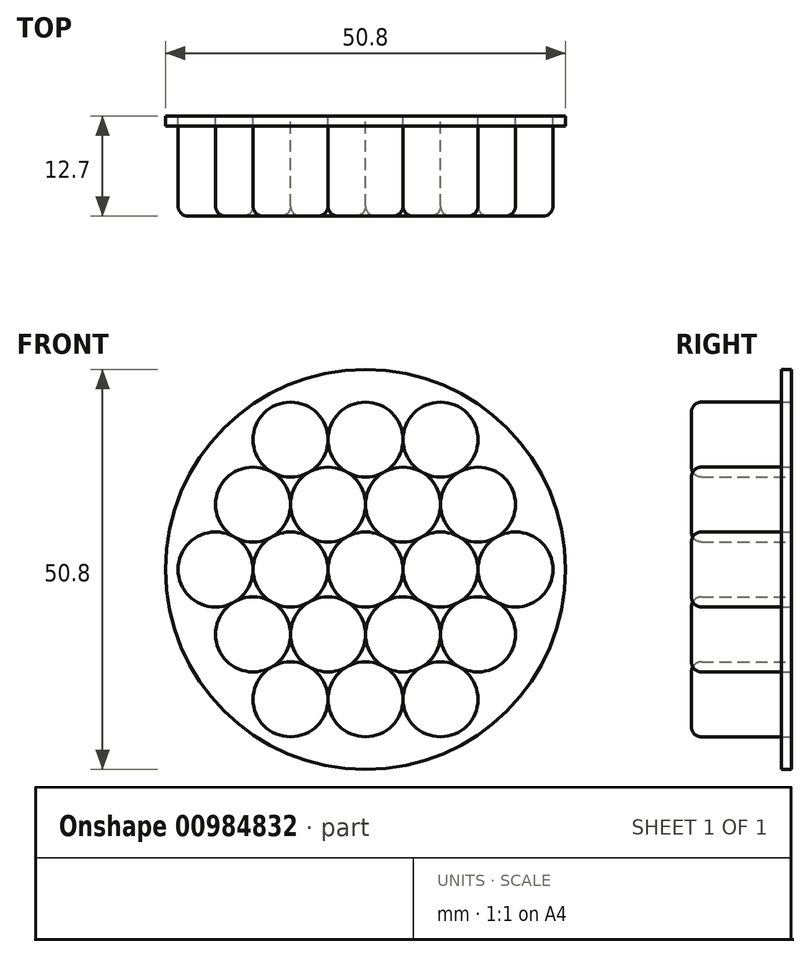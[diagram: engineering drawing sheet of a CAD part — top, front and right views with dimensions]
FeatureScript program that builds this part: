
annotation { "Feature Type Name" : "Feature", "Feature Type Description" : "" }
export const myFeature = defineFeature(function(context is Context, id is Id, definition is map)
    precondition{}
    {
        {
            var Q0;
            Q0=qCreatedBy(makeId("Front.planeOp"),FACE);
            var sketch = newSketch(context, id + "F0", { "sketchPlane" : qUnion([Q0])});
            skCircle(sketch, "E0", {"center": v(0, 0) * mm, "radius": 4.76 * mm});
            skCircle(sketch, "E1", {"center": v(-9.53, 0) * mm, "radius": 4.76 * mm});
            skCircle(sketch, "E2.1.0", {"center": v(-4.76, -8.25) * mm, "radius": 4.76 * mm});
            skCircle(sketch, "E2.2.0", {"center": v(4.76, -8.25) * mm, "radius": 4.76 * mm});
            skCircle(sketch, "E3.1.3.0", {"center": v(9.53, 0) * mm, "radius": 4.76 * mm});
            skCircle(sketch, "E3.1.4.0", {"center": v(4.76, 8.25) * mm, "radius": 4.76 * mm});
            skCircle(sketch, "E3.1.5.0", {"center": v(-4.76, 8.25) * mm, "radius": 4.76 * mm});
            skCircle(sketch, "E4.1.0", {"center": v(-14.29, 8.25) * mm, "radius": 4.76 * mm});
            skCircle(sketch, "E4.2.0", {"center": v(-9.53, 16.5) * mm, "radius": 4.76 * mm});
            skCircle(sketch, "E5.1.0", {"center": v(0, 16.5) * mm, "radius": 4.76 * mm});
            skCircle(sketch, "E5.2.0", {"center": v(9.53, 16.5) * mm, "radius": 4.76 * mm});
            skCircle(sketch, "E6.1.0", {"center": v(14.29, 8.25) * mm, "radius": 4.76 * mm});
            skCircle(sketch, "E6.2.0", {"center": v(19.05, 0) * mm, "radius": 4.76 * mm});
            skCircle(sketch, "E7.1.0", {"center": v(14.29, -8.25) * mm, "radius": 4.76 * mm});
            skCircle(sketch, "E7.2.0", {"center": v(9.52, -16.5) * mm, "radius": 4.76 * mm});
            skCircle(sketch, "E8.1.0", {"center": v(0, -16.5) * mm, "radius": 4.76 * mm});
            skCircle(sketch, "E8.2.0", {"center": v(-9.53, -16.5) * mm, "radius": 4.76 * mm});
            skCircle(sketch, "E9.1.0", {"center": v(-14.29, -8.25) * mm, "radius": 4.76 * mm});
            skCircle(sketch, "E9.2.0", {"center": v(-19.05, 0) * mm, "radius": 4.76 * mm});
            skSolve(sketch);
        }
        {
            var Q0;
            {var subQ0=sQuery(id+"F0.wireOp",EDGE,"E4.2.0");var subQ1=makeQuery(id+"F0.imprint","INTERSECT",VERTEX,{"derivedFrom":[sQuery(id+"F0.wireOp",EDGE,"E4.1.0"),subQ0]});Q0=makeQuery(id+"F0.imprint","IMPRINT",FACE,{"disambiguationData":[TD([[makeQuery(id+"F0.imprint","IMPRINT",EDGE,{"disambiguationData":[TD([[subQ1,-1.0]])],"derivedFrom":subQ0}),1.0]])]});}
            var Q1;
            {var subQ0=sQuery(id+"F0.wireOp",EDGE,"E4.1.0");var subQ1=makeQuery(id+"F0.imprint","INTERSECT",VERTEX,{"derivedFrom":[sQuery(id+"F0.wireOp",EDGE,"E1"),subQ0]});Q1=makeQuery(id+"F0.imprint","IMPRINT",FACE,{"disambiguationData":[TD([[makeQuery(id+"F0.imprint","IMPRINT",EDGE,{"disambiguationData":[TD([[subQ1,-1.0]])],"derivedFrom":subQ0}),1.0]])]});}
            var Q2;
            {var subQ0=sQuery(id+"F0.wireOp",EDGE,"E9.2.0");var subQ1=makeQuery(id+"F0.imprint","INTERSECT",VERTEX,{"derivedFrom":[sQuery(id+"F0.wireOp",EDGE,"E9.1.0"),subQ0]});Q2=makeQuery(id+"F0.imprint","IMPRINT",FACE,{"disambiguationData":[TD([[makeQuery(id+"F0.imprint","IMPRINT",EDGE,{"disambiguationData":[TD([[subQ1,-1.0]])],"derivedFrom":subQ0}),1.0]])]});}
            var Q3;
            {var subQ0=sQuery(id+"F0.wireOp",EDGE,"E9.1.0");var subQ1=makeQuery(id+"F0.imprint","INTERSECT",VERTEX,{"derivedFrom":[sQuery(id+"F0.wireOp",EDGE,"E1"),subQ0]});Q3=makeQuery(id+"F0.imprint","IMPRINT",FACE,{"disambiguationData":[TD([[makeQuery(id+"F0.imprint","IMPRINT",EDGE,{"disambiguationData":[TD([[subQ1,1.0]])],"derivedFrom":subQ0}),1.0]])]});}
            var Q4;
            {var subQ0=sQuery(id+"F0.wireOp",EDGE,"E1");var subQ5=makeQuery(id+"F0.imprint","INTERSECT",VERTEX,{"derivedFrom":[sQuery(id+"F0.wireOp",EDGE,"E0"),subQ0]});Q4=makeQuery(id+"F0.imprint","IMPRINT",FACE,{"disambiguationData":[TD([[makeQuery(id+"F0.imprint","IMPRINT",EDGE,{"disambiguationData":[TD([[subQ5,-1.0]])],"derivedFrom":subQ0}),1.0]])]});}
            var Q5;
            {var subQ0=sQuery(id+"F0.wireOp",EDGE,"E3.1.5.0");var subQ5=makeQuery(id+"F0.imprint","INTERSECT",VERTEX,{"derivedFrom":[sQuery(id+"F0.wireOp",EDGE,"E0"),subQ0]});Q5=makeQuery(id+"F0.imprint","IMPRINT",FACE,{"disambiguationData":[TD([[makeQuery(id+"F0.imprint","IMPRINT",EDGE,{"disambiguationData":[TD([[subQ5,-1.0]])],"derivedFrom":subQ0}),1.0]])]});}
            var Q6;
            {var subQ0=sQuery(id+"F0.wireOp",EDGE,"E5.1.0");var subQ1=makeQuery(id+"F0.imprint","INTERSECT",VERTEX,{"derivedFrom":[sQuery(id+"F0.wireOp",EDGE,"E3.1.4.0"),subQ0]});Q6=makeQuery(id+"F0.imprint","IMPRINT",FACE,{"disambiguationData":[TD([[makeQuery(id+"F0.imprint","IMPRINT",EDGE,{"disambiguationData":[TD([[subQ1,1.0]])],"derivedFrom":subQ0}),1.0]])]});}
            var Q7;
            {var subQ0=sQuery(id+"F0.wireOp",EDGE,"E5.2.0");var subQ1=makeQuery(id+"F0.imprint","INTERSECT",VERTEX,{"derivedFrom":[sQuery(id+"F0.wireOp",EDGE,"E5.1.0"),subQ0]});Q7=makeQuery(id+"F0.imprint","IMPRINT",FACE,{"disambiguationData":[TD([[makeQuery(id+"F0.imprint","IMPRINT",EDGE,{"disambiguationData":[TD([[subQ1,-1.0]])],"derivedFrom":subQ0}),1.0]])]});}
            var Q8;
            {var subQ0=sQuery(id+"F0.wireOp",EDGE,"E3.1.4.0");var subQ5=makeQuery(id+"F0.imprint","INTERSECT",VERTEX,{"derivedFrom":[sQuery(id+"F0.wireOp",EDGE,"E0"),subQ0]});Q8=makeQuery(id+"F0.imprint","IMPRINT",FACE,{"disambiguationData":[TD([[makeQuery(id+"F0.imprint","IMPRINT",EDGE,{"disambiguationData":[TD([[subQ5,-1.0]])],"derivedFrom":subQ0}),1.0]])]});}
            var Q9;
            {var subQ0=sQuery(id+"F0.wireOp",EDGE,"E0");var subQ4=makeQuery(id+"F0.imprint","INTERSECT",VERTEX,{"derivedFrom":[subQ0,sQuery(id+"F0.wireOp",EDGE,"E3.1.4.0")]});Q9=makeQuery(id+"F0.imprint","IMPRINT",FACE,{"disambiguationData":[TD([[makeQuery(id+"F0.imprint","IMPRINT",EDGE,{"disambiguationData":[TD([[subQ4,1.0]])],"derivedFrom":subQ0}),1.0]])]});}
            var Q10;
            {var subQ0=sQuery(id+"F0.wireOp",EDGE,"E2.1.0");var subQ5=makeQuery(id+"F0.imprint","INTERSECT",VERTEX,{"derivedFrom":[sQuery(id+"F0.wireOp",EDGE,"E0"),subQ0]});Q10=makeQuery(id+"F0.imprint","IMPRINT",FACE,{"disambiguationData":[TD([[makeQuery(id+"F0.imprint","IMPRINT",EDGE,{"disambiguationData":[TD([[subQ5,-1.0]])],"derivedFrom":subQ0}),1.0]])]});}
            var Q11;
            {var subQ0=sQuery(id+"F0.wireOp",EDGE,"E8.2.0");var subQ1=makeQuery(id+"F0.imprint","INTERSECT",VERTEX,{"derivedFrom":[sQuery(id+"F0.wireOp",EDGE,"E8.1.0"),subQ0]});Q11=makeQuery(id+"F0.imprint","IMPRINT",FACE,{"disambiguationData":[TD([[makeQuery(id+"F0.imprint","IMPRINT",EDGE,{"disambiguationData":[TD([[subQ1,-1.0]])],"derivedFrom":subQ0}),1.0]])]});}
            var Q12;
            {var subQ0=sQuery(id+"F0.wireOp",EDGE,"E8.1.0");var subQ1=makeQuery(id+"F0.imprint","INTERSECT",VERTEX,{"derivedFrom":[sQuery(id+"F0.wireOp",EDGE,"E2.1.0"),subQ0]});Q12=makeQuery(id+"F0.imprint","IMPRINT",FACE,{"disambiguationData":[TD([[makeQuery(id+"F0.imprint","IMPRINT",EDGE,{"disambiguationData":[TD([[subQ1,1.0]])],"derivedFrom":subQ0}),1.0]])]});}
            var Q13;
            {var subQ0=sQuery(id+"F0.wireOp",EDGE,"E2.2.0");var subQ5=makeQuery(id+"F0.imprint","INTERSECT",VERTEX,{"derivedFrom":[sQuery(id+"F0.wireOp",EDGE,"E0"),subQ0]});Q13=makeQuery(id+"F0.imprint","IMPRINT",FACE,{"disambiguationData":[TD([[makeQuery(id+"F0.imprint","IMPRINT",EDGE,{"disambiguationData":[TD([[subQ5,-1.0]])],"derivedFrom":subQ0}),1.0]])]});}
            var Q14;
            {var subQ0=sQuery(id+"F0.wireOp",EDGE,"E6.1.0");var subQ1=makeQuery(id+"F0.imprint","INTERSECT",VERTEX,{"derivedFrom":[sQuery(id+"F0.wireOp",EDGE,"E3.1.3.0"),subQ0]});Q14=makeQuery(id+"F0.imprint","IMPRINT",FACE,{"disambiguationData":[TD([[makeQuery(id+"F0.imprint","IMPRINT",EDGE,{"disambiguationData":[TD([[subQ1,1.0]])],"derivedFrom":subQ0}),1.0]])]});}
            var Q15;
            {var subQ0=sQuery(id+"F0.wireOp",EDGE,"E3.1.3.0");var subQ5=makeQuery(id+"F0.imprint","INTERSECT",VERTEX,{"derivedFrom":[sQuery(id+"F0.wireOp",EDGE,"E0"),subQ0]});Q15=makeQuery(id+"F0.imprint","IMPRINT",FACE,{"disambiguationData":[TD([[makeQuery(id+"F0.imprint","IMPRINT",EDGE,{"disambiguationData":[TD([[subQ5,-1.0]])],"derivedFrom":subQ0}),1.0]])]});}
            var Q16;
            {var subQ0=sQuery(id+"F0.wireOp",EDGE,"E6.2.0");var subQ1=makeQuery(id+"F0.imprint","INTERSECT",VERTEX,{"derivedFrom":[sQuery(id+"F0.wireOp",EDGE,"E6.1.0"),subQ0]});Q16=makeQuery(id+"F0.imprint","IMPRINT",FACE,{"disambiguationData":[TD([[makeQuery(id+"F0.imprint","IMPRINT",EDGE,{"disambiguationData":[TD([[subQ1,-1.0]])],"derivedFrom":subQ0}),1.0]])]});}
            var Q17;
            {var subQ0=sQuery(id+"F0.wireOp",EDGE,"E7.1.0");var subQ1=makeQuery(id+"F0.imprint","INTERSECT",VERTEX,{"derivedFrom":[sQuery(id+"F0.wireOp",EDGE,"E2.2.0"),subQ0]});Q17=makeQuery(id+"F0.imprint","IMPRINT",FACE,{"disambiguationData":[TD([[makeQuery(id+"F0.imprint","IMPRINT",EDGE,{"disambiguationData":[TD([[subQ1,1.0]])],"derivedFrom":subQ0}),1.0]])]});}
            var Q18;
            {var subQ0=sQuery(id+"F0.wireOp",EDGE,"E7.2.0");var subQ1=makeQuery(id+"F0.imprint","INTERSECT",VERTEX,{"derivedFrom":[sQuery(id+"F0.wireOp",EDGE,"E7.1.0"),subQ0]});Q18=makeQuery(id+"F0.imprint","IMPRINT",FACE,{"disambiguationData":[TD([[makeQuery(id+"F0.imprint","IMPRINT",EDGE,{"disambiguationData":[TD([[subQ1,-1.0]])],"derivedFrom":subQ0}),1.0]])]});}
            extrude(context, id + "F1", {"entities" : qUnion([Q0, Q1, Q2, Q3, Q4, Q5, Q6, Q7, Q8, Q9, Q10, Q11, Q12, Q13, Q14, Q15, Q16, Q17, Q18]), "depth" : 12.7 * mm, "offsetDistance" : 25.4 * mm});
        }
        {
            var Q0;
            Q0=makeQuery(id+"F1.opExtrude","CAP_EDGE",EDGE,{"disambiguationData":[OSD([sQuery(id+"F0.wireOp",EDGE,"E4.2.0")])],"isStart":false});
            var Q1;
            Q1=makeQuery(id+"F1.opExtrude","CAP_EDGE",EDGE,{"disambiguationData":[OSD([sQuery(id+"F0.wireOp",EDGE,"E4.1.0")])],"isStart":false});
            var Q2;
            Q2=makeQuery(id+"F1.opExtrude","CAP_EDGE",EDGE,{"disambiguationData":[OSD([sQuery(id+"F0.wireOp",EDGE,"E9.2.0")])],"isStart":false});
            var Q3;
            Q3=makeQuery(id+"F1.opExtrude","CAP_EDGE",EDGE,{"disambiguationData":[OSD([sQuery(id+"F0.wireOp",EDGE,"E9.1.0")])],"isStart":false});
            var Q4;
            Q4=makeQuery(id+"F1.opExtrude","CAP_EDGE",EDGE,{"disambiguationData":[OSD([sQuery(id+"F0.wireOp",EDGE,"E8.2.0")])],"isStart":false});
            var Q5;
            Q5=makeQuery(id+"F1.opExtrude","CAP_FACE",FACE,{"disambiguationData":[OSD([sQuery(id+"F0.wireOp",EDGE,"E8.1.0")])],"isStart":false});
            var Q6;
            Q6=makeQuery(id+"F1.opExtrude","CAP_EDGE",EDGE,{"disambiguationData":[OSD([sQuery(id+"F0.wireOp",EDGE,"E7.2.0")])],"isStart":false});
            var Q7;
            Q7=makeQuery(id+"F1.opExtrude","CAP_EDGE",EDGE,{"disambiguationData":[OSD([sQuery(id+"F0.wireOp",EDGE,"E7.1.0")])],"isStart":false});
            var Q8;
            Q8=makeQuery(id+"F1.opExtrude","CAP_EDGE",EDGE,{"disambiguationData":[OSD([sQuery(id+"F0.wireOp",EDGE,"E6.2.0")])],"isStart":false});
            var Q9;
            Q9=makeQuery(id+"F1.opExtrude","CAP_EDGE",EDGE,{"disambiguationData":[OSD([sQuery(id+"F0.wireOp",EDGE,"E6.1.0")])],"isStart":false});
            var Q10;
            Q10=makeQuery(id+"F1.opExtrude","CAP_EDGE",EDGE,{"disambiguationData":[OSD([sQuery(id+"F0.wireOp",EDGE,"E5.2.0")])],"isStart":false});
            var Q11;
            Q11=makeQuery(id+"F1.opExtrude","CAP_EDGE",EDGE,{"disambiguationData":[OSD([sQuery(id+"F0.wireOp",EDGE,"E5.1.0")])],"isStart":false});
            var Q12;
            Q12=makeQuery(id+"F1.opExtrude","CAP_EDGE",EDGE,{"disambiguationData":[OSD([sQuery(id+"F0.wireOp",EDGE,"E3.1.4.0")])],"isStart":false});
            var Q13;
            Q13=makeQuery(id+"F1.opExtrude","CAP_EDGE",EDGE,{"disambiguationData":[OSD([sQuery(id+"F0.wireOp",EDGE,"E3.1.3.0")])],"isStart":false});
            var Q14;
            Q14=makeQuery(id+"F1.opExtrude","CAP_EDGE",EDGE,{"disambiguationData":[OSD([sQuery(id+"F0.wireOp",EDGE,"E2.2.0")])],"isStart":false});
            var Q15;
            Q15=makeQuery(id+"F1.opExtrude","CAP_EDGE",EDGE,{"disambiguationData":[OSD([sQuery(id+"F0.wireOp",EDGE,"E0")])],"isStart":false});
            var Q16;
            Q16=makeQuery(id+"F1.opExtrude","CAP_EDGE",EDGE,{"disambiguationData":[OSD([sQuery(id+"F0.wireOp",EDGE,"E3.1.5.0")])],"isStart":false});
            var Q17;
            Q17=makeQuery(id+"F1.opExtrude","CAP_EDGE",EDGE,{"disambiguationData":[OSD([sQuery(id+"F0.wireOp",EDGE,"E1")])],"isStart":false});
            var Q18;
            Q18=makeQuery(id+"F1.opExtrude","CAP_EDGE",EDGE,{"disambiguationData":[OSD([sQuery(id+"F0.wireOp",EDGE,"E2.1.0")])],"isStart":false});
            fillet(context, id + "F2", {"entities" : qUnion([Q0, Q1, Q2, Q3, Q4, Q5, Q6, Q7, Q8, Q9, Q10, Q11, Q12, Q13, Q14, Q15, Q16, Q17, Q18]), "radius" : 1.27 * mm, "tangentPropagation" : true, "allowEdgeOverflow" : false});
        }
        {
            var Q0;
            Q0=qCreatedBy(makeId("Front.planeOp"),FACE);
            var sketch = newSketch(context, id + "F3", { "sketchPlane" : qUnion([Q0])});
            skCircle(sketch, "E10", {"center": v(0, 0) * mm, "radius": 25.4 * mm});
            skSolve(sketch);
        }
        {
            var Q0;
            Q0 = qSketchRegion(id + "F3", true);
            extrude(context, id + "F4", {"entities" : qUnion([Q0]), "depth" : 1.27 * mm, "offsetDistance" : 25.4 * mm});
        }
    });
